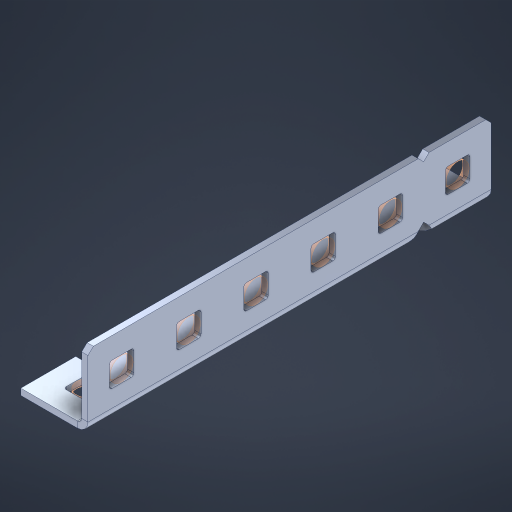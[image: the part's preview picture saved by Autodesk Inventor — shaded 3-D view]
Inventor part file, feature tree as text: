
AUTODESK INVENTOR PART (.ipt)
format: ipt  version: 2023 (Build 270158000, 158)  size: 581,632 bytes
history: native  units: in
note: dims shown in document units (in); Inventor stores cm internally (conversion verified against a paired STEP export)
features: other x25, extrude x16, sheet_metal_op x11, sketch x10, pattern_linear x2, mirror x1, chamfer x1
ambient origin geometry x8: Origin, YZ Plane, XZ Plane, XY Plane, X Axis, Y Axis, Z Axis, Center Point
bodies: Solid1 (feature_tree), Body (feature_tree)
feature tree (66):
  sheet_metal_op  "Flanges"
  other  "Flange Pattern Plane"
  other  "Flange Pattern Sketch"
  sheet_metal_op  "Flange Pattern"
  sheet_metal_op  "Body Pattern"
  pattern_linear  "Center Pattern"  Spacing1=0.0469in  [1 undecoded]
  other  "Arc Length"
  mirror  "Notch Mirror"
  pattern_linear  "Notch Pattern"  Spacing1=0.182in  [1 undecoded]
  chamfer  "End Chamfer"
  extrude  "Half Cut"  Depth=0.02in
  sketch  "Sketch1"  dims[d0=1.0in]
  other  "Plate1"
  sketch  "Sketch2"  dims[d1=3.0in]
  other  "Plate2"
  sheet_metal_op  "Bend1"
  sheet_metal_op  "Corner1"
  sketch  "Sketch3"  dims[d2=0.0469in]
  sketch  "Sketch7"  dims[d3=0.0469in]
  other  "Srf1"
  other  "Srf2"
  sketch  "Sketch8"  dims[d4=0.0234in]
  sketch  "Sketch9"  dims[d5=0.0938in]
  other  "Srf91"
  sheet_metal_op  "Body Pattern Sketch"
  other  "Srf92"
  sketch  "Sketch13"  dims[d6=0.0469in]
  sketch  "Sketch14"  dims[d7=0.5in d8=90.0deg d9=0.0312in]
  sketch  "Sketch15"  dims[d10=0.1875in]
  sketch  "Sketch16"  dims[d11=0.0469in d12=0.0469in d16=0.182in d17=0.02in d18=0.0469in d19=0.0in d20=0.25in d21=0.25in d38=2.3622in d40=0.5in d41=0.3937in d43=1.0in d46=0.172in d47=1.0in d48=0.0in d49=0.182in d50=0.02in d51=0.25in d52=0.25in d53=0.0469in d54=0.0in d55=0.172in d56=1.0in d57=0.0in d58=0.25in d60=2.3622in d62=0.5in d63=0.3937in d65=0.5in d85=0.1227in d86=0.1659in d88=0.04in d89=0.0469in d90=0.0in d91=0.04in d92=0.0491in d95=2.5in d96=0.04in d97=0.25in d98=45.0deg d99=0.25in d100=0.5in d101=0.0in d102=2.497in d106=0.182in d107=0.02in d108=0.5in d109=0.5in d110=0.0469in d111=0.0in d112=0.172in d113=0.5in d114=0.0in d117=0.5in d118=0.5in d119=0.5in]
  other  "Srf786"
  other  "Srf823"
  other  "Srf824"
  other  "Srf825"
  other  "Srf826"
  other  "Srf856"
  other  "Srf857"
  other  "Srf858"
  other  "Srf859"
  other  "Srf889"
  other  "Srf890"
  other  "Srf891"
  other  "Srf892"
  other  "Srf893"
  sheet_metal_op  "Flange Stamp"
  sheet_metal_op  "Flange Circle"
  sheet_metal_op  "Body Stamp"
  sheet_metal_op  "Body Circle"
  other  "Center Stamp"
  other  "Center Circle"
  sheet_metal_op  "Notch"
  extrude  "ExtrusionSrf2"  Depth=0.0469in
  extrude  "ExtrusionSrf92"  TaperAngle=0.0deg  [1 undecoded]
  extrude  "ExtrusionSrf823"  Depth=0.25in
  extrude  "ExtrusionSrf824"  Depth=0.25in
  extrude  "ExtrusionSrf825"  Depth=0.5in
  extrude  "ExtrusionSrf826"  Depth=0.5in
  extrude  "ExtrusionSrf856"  Depth=1.0in TaperAngle=0.0deg
  extrude  "ExtrusionSrf857"  Depth=0.182in
  extrude  "ExtrusionSrf858"  Depth=0.02in
  extrude  "ExtrusionSrf859"  Depth=0.25in
  extrude  "ExtrusionSrf889"  Depth=0.25in
  extrude  "ExtrusionSrf890"  Depth=0.0469in
  extrude  "ExtrusionSrf891"  TaperAngle=0.0deg  [1 undecoded]
  extrude  "ExtrusionSrf892"  Depth=0.5in
  extrude  "ExtrusionSrf893"  Depth=1.0in TaperAngle=0.0deg
note: 4 required parameter values undecoded (feature->parameter linkage not recoverable at this tier; creation-order binding heuristic only, values carry confidence <= 0.55)
